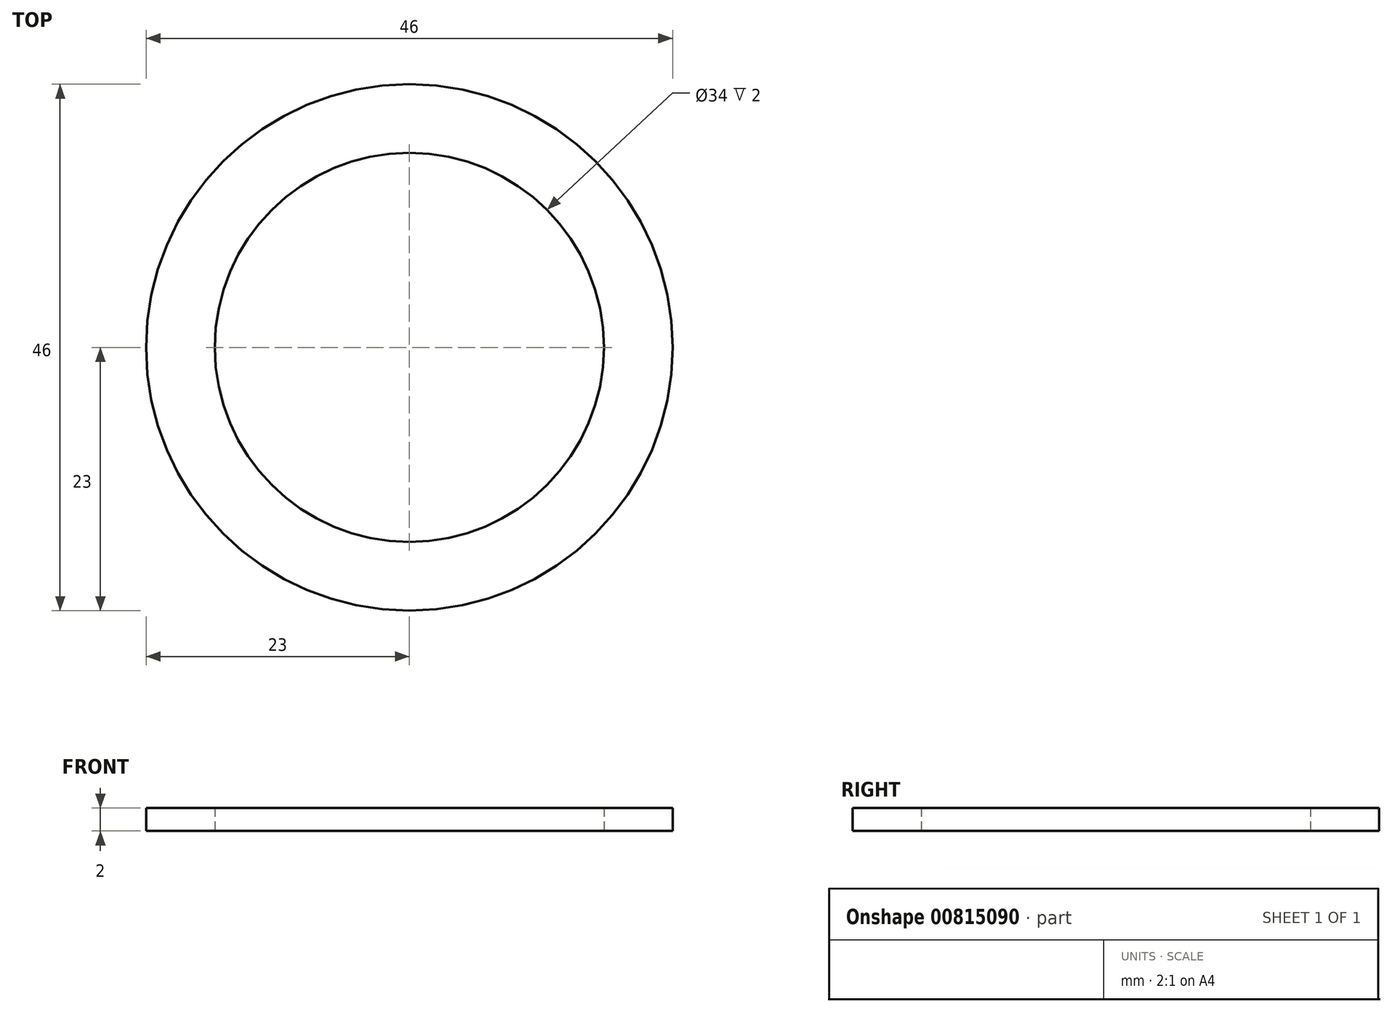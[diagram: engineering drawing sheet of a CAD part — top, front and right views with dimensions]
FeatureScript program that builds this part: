
annotation { "Feature Type Name" : "Feature", "Feature Type Description" : "" }
export const myFeature = defineFeature(function(context is Context, id is Id, definition is map)
    precondition{}
    {
        {
            var Q0;
            Q0=qCreatedBy(makeId("Front.planeOp"),FACE);
            var sketch = newSketch(context, id + "F0", { "sketchPlane" : qUnion([Q0])});
            skLineSegment(sketch, "E0", {"start": v(-17, 0) * mm, "end": v(-23, 0) * mm});
            skLineSegment(sketch, "E1", {"start": v(-23, 0) * mm, "end": v(-23, 2) * mm});
            skLineSegment(sketch, "E2", {"start": v(-23, 2) * mm, "end": v(-17, 2) * mm});
            skLineSegment(sketch, "E3", {"start": v(-17, 2) * mm, "end": v(-17, 0) * mm});
            skLineSegment(sketch, "E4", {"start": v(0, 0.84) * mm, "end": v(0, 3.37) * mm});
            skSolve(sketch);
        }
        {
            var Q0;
            Q0 = qSketchRegion(id + "F0", true);
            var Q1;
            Q1=sQuery(id+"F0.wireOp",EDGE,"E4");
            revolve(context, id + "F1", {"surfaceOperationType" : NewSurfaceOperationType.NEW, "entities" : qUnion([Q0]), "axis" : qUnion([Q1]), "revolveType" : RevolveType.FULL});
        }
    });
